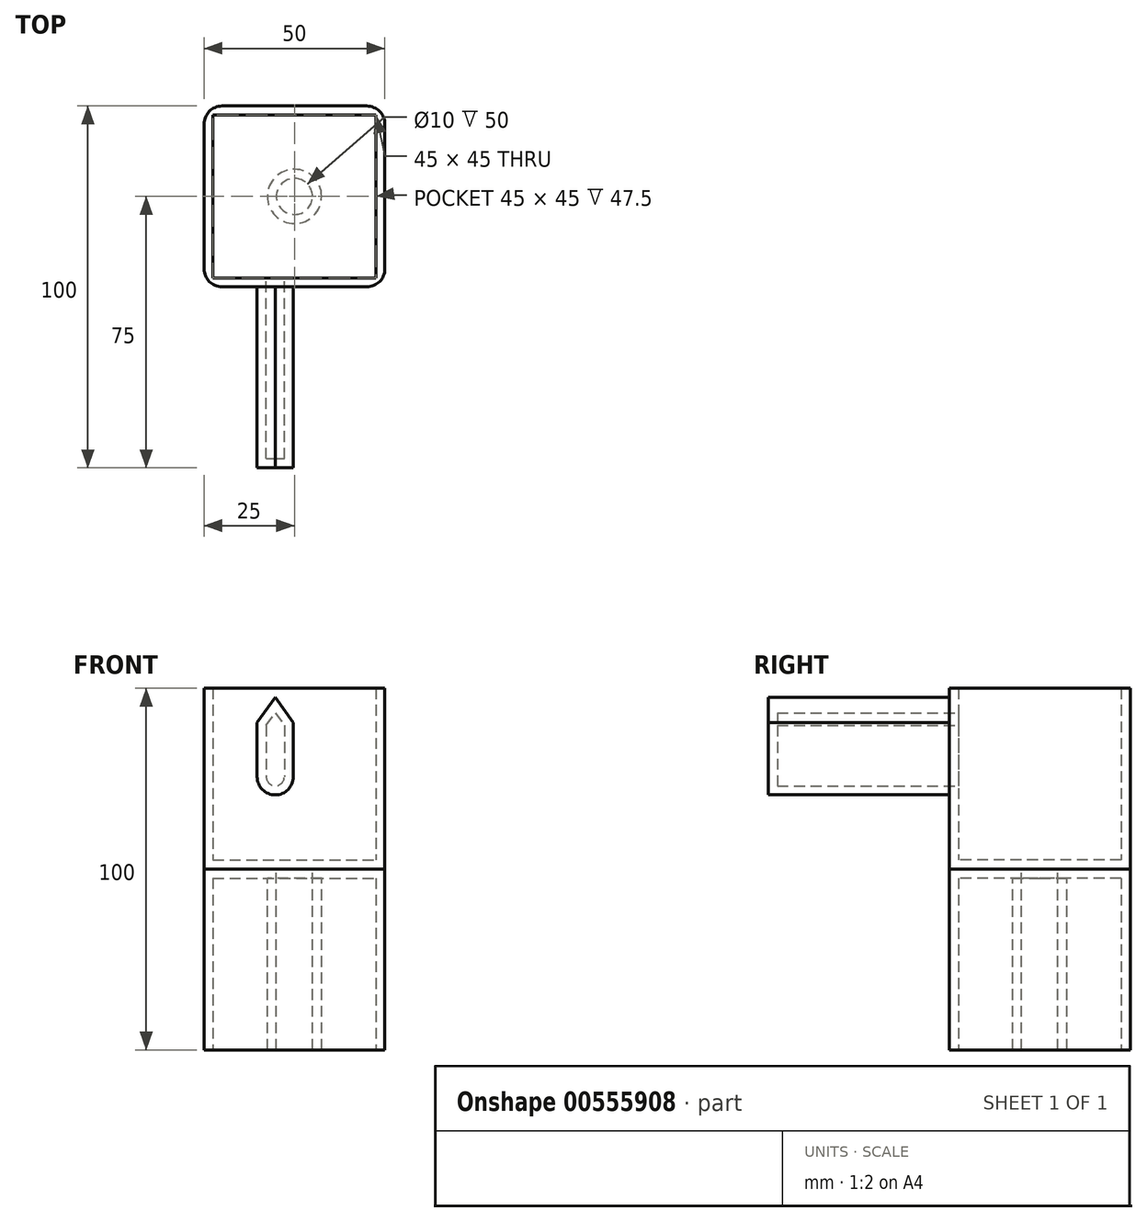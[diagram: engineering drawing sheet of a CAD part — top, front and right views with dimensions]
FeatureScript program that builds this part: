
annotation { "Feature Type Name" : "Feature", "Feature Type Description" : "" }
export const myFeature = defineFeature(function(context is Context, id is Id, definition is map)
    precondition{}
    {
        {
            var Q0;
            Q0=qCreatedBy(makeId("Top.planeOp"),FACE);
            var sketch = newSketch(context, id + "F0", { "sketchPlane" : qUnion([Q0])});
            skLineSegment(sketch, "E0.bottom", {"start": v(-50, 0) * mm, "end": v(0, 0) * mm});
            skLineSegment(sketch, "E0.top", {"start": v(-50, -50) * mm, "end": v(0, -50) * mm});
            skLineSegment(sketch, "E0.left", {"start": v(-50, 0) * mm, "end": v(-50, -50) * mm});
            skLineSegment(sketch, "E0.right", {"start": v(0, 0) * mm, "end": v(0, -50) * mm});
            skSolve(sketch);
        }
        {
            var Q0;
            Q0 = qSketchRegion(id + "F0", true);
            extrude(context, id + "F1", {"entities" : qUnion([Q0]), "depth" : 50 * mm, "offsetDistance" : 25 * mm});
        }
        {
            var Q0;
            Q0=makeQuery(id+"F1.opExtrude","CAP_FACE",FACE,{"disambiguationData":[OSD([sQuery(id+"F0.wireOp",EDGE,"E0.bottom"),sQuery(id+"F0.wireOp",EDGE,"E0.top"),sQuery(id+"F0.wireOp",EDGE,"E0.left"),sQuery(id+"F0.wireOp",EDGE,"E0.right")])],"isStart":false});
            var sketch = newSketch(context, id + "F2", { "sketchPlane" : qUnion([Q0])});
            skCircle(sketch, "E1", {"center": v(-25, -25) * mm, "radius": 5 * mm});
            skSolve(sketch);
        }
        {
            var Q0;
            Q0 = qSketchRegion(id + "F2", true);
            extrude(context, id + "F3", {"entities" : qUnion([Q0]), "operationType" : NewBodyOperationType.REMOVE, "oppositeDirection" : true, "depth" : 50 * mm, "offsetDistance" : 25 * mm});
        }
        {
            var Q0;
            Q0=makeQuery(id+"F1.opExtrude","CAP_FACE",FACE,{"disambiguationData":[OSD([sQuery(id+"F0.wireOp",EDGE,"E0.bottom"),sQuery(id+"F0.wireOp",EDGE,"E0.top"),sQuery(id+"F0.wireOp",EDGE,"E0.left"),sQuery(id+"F0.wireOp",EDGE,"E0.right")])],"isStart":false});
            var sketch = newSketch(context, id + "F4", { "sketchPlane" : qUnion([Q0])});
            skLineSegment(sketch, "E2.bottom", {"start": v(-50, -50) * mm, "end": v(0, -50) * mm});
            skLineSegment(sketch, "E2.top", {"start": v(-50, 0) * mm, "end": v(0, 0) * mm});
            skLineSegment(sketch, "E2.left", {"start": v(-50, -50) * mm, "end": v(-50, 0) * mm});
            skLineSegment(sketch, "E2.right", {"start": v(0, -50) * mm, "end": v(0, 0) * mm});
            skSolve(sketch);
        }
        {
            var Q0;
            Q0 = qSketchRegion(id + "F4", true);
            extrude(context, id + "F5", {"entities" : qUnion([Q0]), "depth" : 50 * mm, "offsetDistance" : 25 * mm});
        }
        {
            var Q0;
            Q0=makeQuery(id+"F5.opExtrude","SWEPT_FACE",FACE,{"disambiguationData":[OSD([sQuery(id+"F4.wireOp",EDGE,"E2.bottom")])]});
            var sketch = newSketch(context, id + "F6", { "sketchPlane" : qUnion([Q0])});
            skLineSegment(sketch, "E3.left", {"start": v(-35.31, 90.5) * mm, "end": v(-35.31, 75.5) * mm});
            skLineSegment(sketch, "E3.right", {"start": v(-25.31, 90.5) * mm, "end": v(-25.31, 75.5) * mm});
            skArc(sketch, "E4", {"start": v(-35.31, 75.5) * mm, "mid": v(-30.31, 70.5) * mm, "end": v(-25.31, 75.5) * mm});
            skLineSegment(sketch, "E5", {"start": v(-35.31, 90.5) * mm, "end": v(-30.31, 97.5) * mm});
            skPoint(sketch, "E5.endSnap0", {"position": v(-30.31, 90.5) * mm});
            skLineSegment(sketch, "E6", {"start": v(-30.31, 97.5) * mm, "end": v(-25.31, 90.5) * mm});
            skSolve(sketch);
        }
        {
            var Q0;
            Q0 = qSketchRegion(id + "F6", true);
            extrude(context, id + "F7", {"entities" : qUnion([Q0]), "operationType" : NewBodyOperationType.ADD, "depth" : 50 * mm, "offsetDistance" : 25 * mm});
        }
        {
            var Q0;
            Q0=makeQuery(id+"F1.opExtrude","CAP_FACE",FACE,{"disambiguationData":[OSD([sQuery(id+"F0.wireOp",EDGE,"E0.bottom"),sQuery(id+"F0.wireOp",EDGE,"E0.top"),sQuery(id+"F0.wireOp",EDGE,"E0.left"),sQuery(id+"F0.wireOp",EDGE,"E0.right")])],"isStart":true});
            shell(context, id + "F8", {"entities" : qUnion([Q0]), "thickness" : 2.5 * mm});
        }
        {
            var Q0;
            Q0=makeQuery(id+"F1.opExtrude","SWEPT_EDGE",EDGE,{"disambiguationData":[OSD([sQuery(id+"F0.wireOp",EDGE,"E0.top"),sQuery(id+"F0.wireOp",EDGE,"E0.left")])]});
            var Q1;
            Q1=makeQuery(id+"F1.opExtrude","SWEPT_EDGE",EDGE,{"disambiguationData":[OSD([sQuery(id+"F0.wireOp",EDGE,"E0.bottom"),sQuery(id+"F0.wireOp",EDGE,"E0.left")])]});
            var Q2;
            Q2=makeQuery(id+"F1.opExtrude","SWEPT_EDGE",EDGE,{"disambiguationData":[OSD([sQuery(id+"F0.wireOp",EDGE,"E0.top"),sQuery(id+"F0.wireOp",EDGE,"E0.right")])]});
            var Q3;
            Q3=makeQuery(id+"F1.opExtrude","SWEPT_EDGE",EDGE,{"disambiguationData":[OSD([sQuery(id+"F0.wireOp",EDGE,"E0.bottom"),sQuery(id+"F0.wireOp",EDGE,"E0.right")])]});
            fillet(context, id + "F9", {"entities" : qUnion([Q0, Q1, Q2, Q3]), "radius" : 5 * mm, "tangentPropagation" : true, "allowEdgeOverflow" : false});
        }
        {
            var Q0;
            Q0=makeQuery(id+"F5.opExtrude","CAP_FACE",FACE,{"disambiguationData":[OSD([sQuery(id+"F4.wireOp",EDGE,"E2.bottom"),sQuery(id+"F4.wireOp",EDGE,"E2.top"),sQuery(id+"F4.wireOp",EDGE,"E2.left"),sQuery(id+"F4.wireOp",EDGE,"E2.right")])],"isStart":false});
            shell(context, id + "F10", {"entities" : qUnion([Q0]), "thickness" : 2.5 * mm});
        }
        {
            var Q0;
            Q0=makeQuery(id+"F5.opExtrude","SWEPT_EDGE",EDGE,{"disambiguationData":[OSD([sQuery(id+"F4.wireOp",EDGE,"E2.top"),sQuery(id+"F4.wireOp",EDGE,"E2.left")])]});
            var Q1;
            Q1=makeQuery(id+"F5.opExtrude","SWEPT_EDGE",EDGE,{"disambiguationData":[OSD([sQuery(id+"F4.wireOp",EDGE,"E2.bottom"),sQuery(id+"F4.wireOp",EDGE,"E2.left")])]});
            var Q2;
            Q2=makeQuery(id+"F5.opExtrude","SWEPT_EDGE",EDGE,{"disambiguationData":[OSD([sQuery(id+"F4.wireOp",EDGE,"E2.top"),sQuery(id+"F4.wireOp",EDGE,"E2.right")])]});
            var Q3;
            Q3=makeQuery(id+"F5.opExtrude","SWEPT_EDGE",EDGE,{"disambiguationData":[OSD([sQuery(id+"F4.wireOp",EDGE,"E2.bottom"),sQuery(id+"F4.wireOp",EDGE,"E2.right")])]});
            fillet(context, id + "F11", {"entities" : qUnion([Q0, Q1, Q2, Q3]), "radius" : 5 * mm, "tangentPropagation" : true, "allowEdgeOverflow" : false});
        }
    });
